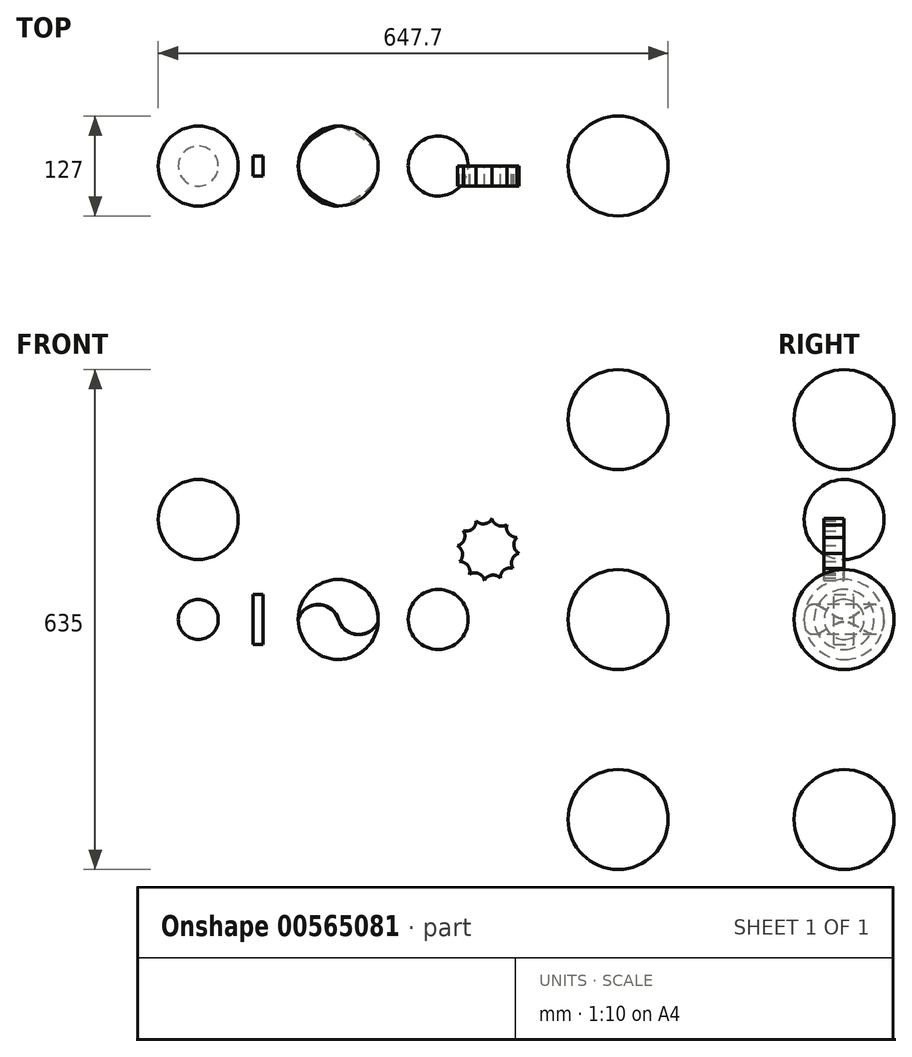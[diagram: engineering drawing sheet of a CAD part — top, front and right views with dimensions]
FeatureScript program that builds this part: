
annotation { "Feature Type Name" : "Feature", "Feature Type Description" : "" }
export const myFeature = defineFeature(function(context is Context, id is Id, definition is map)
    precondition{}
    {
        {
            var Q0;
            Q0=qCreatedBy(makeId("Front.planeOp"),FACE);
            var sketch = newSketch(context, id + "F0", { "sketchPlane" : qUnion([Q0])});
            skLineSegment(sketch, "E0", {"start": v(0, 0) * mm, "end": v(0, 127) * mm, "construction": true});
            skArc(sketch, "E1", {"start": v(0, 76.2) * mm, "mid": v(50.8, 127) * mm, "end": v(0, 177.8) * mm});
            skLineSegment(sketch, "E2", {"start": v(0, 177.8) * mm, "end": v(0, 76.2) * mm});
            skSolve(sketch);
        }
        {
            var Q0;
            Q0=makeQuery(id+"F0.imprint","IMPRINT",FACE,{"disambiguationData":[TD([[makeQuery(id+"F0.imprint","IMPRINT",EDGE,{"derivedFrom":sQuery(id+"F0.wireOp",EDGE,"E1")}),1.0]])]});
            var Q1;
            Q1=sQuery(id+"F0.wireOp",EDGE,"E2");
            revolve(context, id + "F1", {"entities" : qUnion([Q0]), "axis" : qUnion([Q1]), "revolveType" : RevolveType.FULL});
        }
        {
            var Q0;
            Q0=qCreatedBy(makeId("Front.planeOp"),FACE);
            var sketch = newSketch(context, id + "F2", { "sketchPlane" : qUnion([Q0])});
            skArc(sketch, "E3", {"start": v(0, -25.4) * mm, "mid": v(25.4, 0) * mm, "end": v(0, 25.4) * mm});
            skLineSegment(sketch, "E4", {"start": v(0, 25.4) * mm, "end": v(0, -25.4) * mm});
            skSolve(sketch);
        }
        {
            var Q0;
            Q0=makeQuery(id+"F2.imprint","IMPRINT",FACE,{"disambiguationData":[TD([[makeQuery(id+"F2.imprint","IMPRINT",EDGE,{"derivedFrom":sQuery(id+"F2.wireOp",EDGE,"E3")}),1.0]])]});
            var Q1;
            Q1=sQuery(id+"F2.wireOp",EDGE,"E4");
            revolve(context, id + "F3", {"entities" : qUnion([Q0]), "axis" : qUnion([Q1]), "revolveType" : RevolveType.FULL});
        }
        {
            var Q0;
            Q0=qCreatedBy(makeId("Front.planeOp"),FACE);
            var sketch = newSketch(context, id + "F4", { "sketchPlane" : qUnion([Q0])});
            skLineSegment(sketch, "E5", {"start": v(0, 0) * mm, "end": v(76.2, 0) * mm, "construction": true});
            skLineSegment(sketch, "E6.bottom", {"start": v(82.55, -31.75) * mm, "end": v(69.85, -31.75) * mm});
            skLineSegment(sketch, "E6.top", {"start": v(82.55, 31.75) * mm, "end": v(69.85, 31.75) * mm});
            skLineSegment(sketch, "E6.left", {"start": v(82.55, -31.75) * mm, "end": v(82.55, 31.75) * mm});
            skLineSegment(sketch, "E6.right", {"start": v(69.85, -31.75) * mm, "end": v(69.85, 31.75) * mm});
            skPoint(sketch, "E6.middle", {"position": v(76.2, 0) * mm});
            skSolve(sketch);
        }
        {
            var Q0;
            Q0 = qSketchRegion(id + "F4", true);
            extrude(context, id + "F5", {"entities" : qUnion([Q0]), "endBound" : BoundingType.SYMMETRIC, "depth" : 25.4 * mm, "offsetDistance" : 25.4 * mm});
        }
        {
            var Q0;
            Q0=qCreatedBy(makeId("Front.planeOp"),FACE);
            var sketch = newSketch(context, id + "F6", { "sketchPlane" : qUnion([Q0])});
            skLineSegment(sketch, "E7", {"start": v(0, 0) * mm, "end": v(177.8, 0) * mm, "construction": true});
            skArc(sketch, "E8", {"start": v(177.8, -50.8) * mm, "mid": v(228.6, 0) * mm, "end": v(177.8, 50.8) * mm});
            skLineSegment(sketch, "E9", {"start": v(177.8, 50.8) * mm, "end": v(177.8, -50.8) * mm});
            skSolve(sketch);
        }
        {
            var Q0;
            Q0 = qSketchRegion(id + "F6", true);
            var Q1;
            Q1=sQuery(id+"F6.wireOp",EDGE,"E9");
            revolve(context, id + "F7", {"entities" : qUnion([Q0]), "axis" : qUnion([Q1]), "revolveType" : RevolveType.FULL});
        }
        {
            var Q0;
            Q0=qCreatedBy(makeId("Front.planeOp"),FACE);
            var sketch = newSketch(context, id + "F8", { "sketchPlane" : qUnion([Q0])});
            skCircle(sketch, "E10", {"center": v(177.8, 0) * mm, "radius": 50.8 * mm});
            skArc(sketch, "E11", {"start": v(177.8, 0) * mm, "mid": v(152.4, 18.79) * mm, "end": v(127, 0) * mm});
            skArc(sketch, "E12", {"start": v(177.8, 0) * mm, "mid": v(201.89, -19.19) * mm, "end": v(228.47, -3.63) * mm});
            skLineSegment(sketch, "E13", {"start": v(127, 0) * mm, "end": v(229.87, 0) * mm, "construction": true});
            skArc(sketch, "E14.0", {"start": v(178.04, 0.07) * mm, "mid": v(152.8, 19.04) * mm, "end": v(127, 0.85) * mm});
            skArc(sketch, "E14.1", {"start": v(178.04, 0.07) * mm, "mid": v(202.24, -18.96) * mm, "end": v(228.52, -2.92) * mm});
            skSolve(sketch);
        }
        {
            var Q0;
            {var subQ0=sQuery(id+"F8.wireOp",EDGE,"E11");Q0=makeQuery(id+"F8.imprint","IMPRINT",FACE,{"disambiguationData":[TD([[makeQuery(id+"F8.imprint","IMPRINT",EDGE,{"derivedFrom":subQ0}),-1.0]])]});}
            extrude(context, id + "F9", {"entities" : qUnion([Q0]), "operationType" : NewBodyOperationType.REMOVE, "endBound" : BoundingType.SYMMETRIC, "oppositeDirection" : true, "depth" : 3048 * mm, "offsetDistance" : 25.4 * mm});
        }
        {
            var Q0;
            Q0=qCreatedBy(makeId("Front.planeOp"),FACE);
            var sketch = newSketch(context, id + "F10", { "sketchPlane" : qUnion([Q0])});
            skLineSegment(sketch, "E15", {"start": v(0, 0) * mm, "end": v(304.8, 0) * mm, "construction": true});
            skArc(sketch, "E16", {"start": v(304.8, -38.1) * mm, "mid": v(342.9, 0) * mm, "end": v(304.8, 38.1) * mm});
            skLineSegment(sketch, "E17", {"start": v(304.8, 38.1) * mm, "end": v(304.8, -38.1) * mm});
            skSolve(sketch);
        }
        {
            var Q0;
            Q0 = qSketchRegion(id + "F10", true);
            var Q1;
            Q1=sQuery(id+"F10.wireOp",EDGE,"E17");
            revolve(context, id + "F11", {"entities" : qUnion([Q0]), "axis" : qUnion([Q1]), "revolveType" : RevolveType.FULL});
        }
        {
            var Q0;
            Q0=qCreatedBy(makeId("Front.planeOp"),FACE);
            var sketch = newSketch(context, id + "F12", { "sketchPlane" : qUnion([Q0])});
            skLineSegment(sketch, "E18", {"start": v(0, 0) * mm, "end": v(368.3, 0) * mm, "construction": true});
            skLineSegment(sketch, "E19", {"start": v(368.3, 0) * mm, "end": v(368.3, 88.9) * mm, "construction": true});
            skCircle(sketch, "E20.cCircle", {"center": v(368.3, 88.9) * mm, "radius": 38.1 * mm, "construction": true});
            skLineSegment(sketch, "E20.0", {"start": v(373.14, 128.05) * mm, "end": v(392.06, 120.38) * mm});
            skLineSegment(sketch, "E20.1", {"start": v(392.06, 120.38) * mm, "end": v(404.62, 104.28) * mm});
            skLineSegment(sketch, "E20.2", {"start": v(404.62, 104.28) * mm, "end": v(407.45, 84.06) * mm});
            skLineSegment(sketch, "E20.3", {"start": v(407.45, 84.06) * mm, "end": v(399.78, 65.14) * mm});
            skLineSegment(sketch, "E20.4", {"start": v(399.78, 65.14) * mm, "end": v(383.68, 52.58) * mm});
            skLineSegment(sketch, "E20.5", {"start": v(383.68, 52.58) * mm, "end": v(363.46, 49.75) * mm});
            skLineSegment(sketch, "E20.6", {"start": v(363.46, 49.75) * mm, "end": v(344.54, 57.42) * mm});
            skLineSegment(sketch, "E20.7", {"start": v(344.54, 57.42) * mm, "end": v(331.98, 73.52) * mm});
            skLineSegment(sketch, "E20.8", {"start": v(331.98, 73.52) * mm, "end": v(329.15, 93.74) * mm});
            skLineSegment(sketch, "E20.9", {"start": v(329.15, 93.74) * mm, "end": v(336.82, 112.66) * mm});
            skLineSegment(sketch, "E20.10", {"start": v(336.82, 112.66) * mm, "end": v(352.92, 125.22) * mm});
            skLineSegment(sketch, "E20.11", {"start": v(352.92, 125.22) * mm, "end": v(373.14, 128.05) * mm});
            skPoint(sketch, "E20.0.midPoint", {"position": v(382.6, 124.21) * mm});
            skArc(sketch, "E21", {"start": v(352.92, 125.22) * mm, "mid": v(363.74, 121.54) * mm, "end": v(373.14, 128.05) * mm});
            skArc(sketch, "E22", {"start": v(373.14, 128.05) * mm, "mid": v(380.67, 119.45) * mm, "end": v(392.06, 120.38) * mm});
            skArc(sketch, "E23", {"start": v(392.06, 120.38) * mm, "mid": v(394.28, 109.17) * mm, "end": v(404.62, 104.28) * mm});
            skArc(sketch, "E24", {"start": v(404.62, 104.28) * mm, "mid": v(400.94, 93.46) * mm, "end": v(407.45, 84.06) * mm});
            skArc(sketch, "E25", {"start": v(407.45, 84.06) * mm, "mid": v(398.85, 76.53) * mm, "end": v(399.78, 65.14) * mm});
            skArc(sketch, "E26", {"start": v(399.78, 65.14) * mm, "mid": v(388.57, 62.92) * mm, "end": v(383.68, 52.58) * mm});
            skArc(sketch, "E27", {"start": v(383.68, 52.58) * mm, "mid": v(372.86, 56.26) * mm, "end": v(363.46, 49.75) * mm});
            skArc(sketch, "E28", {"start": v(363.46, 49.75) * mm, "mid": v(355.93, 58.35) * mm, "end": v(344.54, 57.42) * mm});
            skArc(sketch, "E29", {"start": v(344.54, 57.42) * mm, "mid": v(342.32, 68.63) * mm, "end": v(331.98, 73.52) * mm});
            skArc(sketch, "E30", {"start": v(331.98, 73.52) * mm, "mid": v(335.66, 84.34) * mm, "end": v(329.15, 93.74) * mm});
            skArc(sketch, "E31", {"start": v(329.15, 93.74) * mm, "mid": v(337.75, 101.27) * mm, "end": v(336.82, 112.66) * mm});
            skArc(sketch, "E32", {"start": v(336.82, 112.66) * mm, "mid": v(348.03, 114.88) * mm, "end": v(352.92, 125.22) * mm});
            skSolve(sketch);
        }
        {
            var Q0;
            Q0=makeQuery(id+"F12.imprint","IMPRINT",FACE,{"disambiguationData":[TD([[makeQuery(id+"F12.imprint","IMPRINT",EDGE,{"derivedFrom":sQuery(id+"F12.wireOp",EDGE,"E21")}),-1.0]])]});
            extrude(context, id + "F13", {"entities" : qUnion([Q0]), "depth" : 25.4 * mm, "offsetDistance" : 25.4 * mm});
        }
        {
            var Q0;
            Q0=qCreatedBy(makeId("Front.planeOp"),FACE);
            var sketch = newSketch(context, id + "F14", { "sketchPlane" : qUnion([Q0])});
            skLineSegment(sketch, "E33", {"start": v(0, 0) * mm, "end": v(533.4, 0) * mm, "construction": true});
            skLineSegment(sketch, "E34", {"start": v(533.4, 0) * mm, "end": v(533.4, 254) * mm, "construction": true});
            skArc(sketch, "E35", {"start": v(533.4, 190.5) * mm, "mid": v(596.9, 254) * mm, "end": v(533.4, 317.5) * mm});
            skLineSegment(sketch, "E36", {"start": v(533.4, 317.5) * mm, "end": v(533.4, 190.5) * mm});
            skSolve(sketch);
        }
        {
            var Q0;
            Q0 = qSketchRegion(id + "F14", true);
            var Q1;
            Q1=sQuery(id+"F14.wireOp",EDGE,"E34");
            revolve(context, id + "F15", {"entities" : qUnion([Q0]), "axis" : qUnion([Q1]), "revolveType" : RevolveType.FULL});
        }
        {
            var Q0;
            Q0=makeQuery(id+"F15.opRevolve","SWEPT_BODY",BODY,{"disambiguationData":[OSD([sQuery(id+"F14.wireOp",EDGE,"E35"),sQuery(id+"F14.wireOp",EDGE,"E36")])]});
            var Q1;
            Q1=makeQuery(id+"F15.opRevolve","SWEPT_FACE",FACE,{"disambiguationData":[OSD([sQuery(id+"F14.wireOp",EDGE,"E35")])]});
            var Q2;
            Q2=qCreatedBy(makeId("Top.planeOp"),FACE);
            mirror(context, id + "F16", {"patternType" : MirrorType.FACE, "entities" : qUnion([Q0]), "faces" : qUnion([Q1]), "mirrorPlane" : qUnion([Q2])});
        }
        {
            var Q0;
            Q0=qCreatedBy(makeId("Front.planeOp"),FACE);
            var sketch = newSketch(context, id + "F17", { "sketchPlane" : qUnion([Q0])});
            skArc(sketch, "E37", {"start": v(533.4, -63.5) * mm, "mid": v(596.9, 0) * mm, "end": v(533.4, 63.5) * mm});
            skLineSegment(sketch, "E38", {"start": v(533.4, 63.5) * mm, "end": v(533.4, -63.5) * mm});
            skSolve(sketch);
        }
        {
            var Q0;
            Q0 = qSketchRegion(id + "F17", true);
            var Q1;
            Q1=sQuery(id+"F17.wireOp",EDGE,"E38");
            revolve(context, id + "F18", {"entities" : qUnion([Q0]), "axis" : qUnion([Q1]), "revolveType" : RevolveType.FULL});
        }
    });
